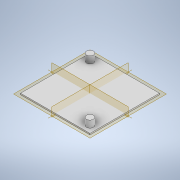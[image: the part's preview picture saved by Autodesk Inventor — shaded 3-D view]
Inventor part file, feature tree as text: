
AUTODESK INVENTOR PART (.ipt)
format: ipt  version: 2022.4 (Build 264492010, 492A)  size: 113,152 bytes
history: native  units: mm
features: extrude x2, sketch x2
ambient origin geometry x8: Origin, YZ Plane, XZ Plane, XY Plane, X Axis, Y Axis, Z Axis, Center Point
bodies: Solid1 (feature_tree)
feature tree (4):
  extrude  "Extrusion1"  Depth=50.0mm
  extrude  "Extrusion2"  Depth=5.0mm
  sketch  "Sketch1"  dims[d0=50.0mm d1=50.0mm]
  sketch  "Sketch2"  dims[d2=1.0mm d3=0.0mm d4=5.0mm d5=5.0mm d6=5.0mm d7=20.0mm d9=360.0deg d11=5.0mm d12=0.0mm]
